FREECAD ASSEMBLY — COMPONENT RECIPES ("generated_example_K93-10436_all7_withDockLinkFrame")

This assembly document has 15 components, labeled P0..P14 below (a component is one placed body or linked part). 1 of them carries a construction recipe — the FreeCAD feature program that regenerates the part from scratch, quoted from this document or its linked companion documents; the rest are supplied as boundary geometry only. No exploded tour is included for this assembly.
COMPONENT P0 — geometry summary ("Body"; no construction recipe available for this part):
  bounding box: 104.0 x 36.0 x 1.5 mm
  tessellated surface: 8,624 triangles
  volume: 4912 mm^3 (87% of its bounding box)
  symmetry: mirror-symmetric across its y mid-plane
COMPONENT P1 — geometry summary ("Body001"; no construction recipe available for this part):
  bounding box: 36.0 x 20.0 x 8.6 mm
  tessellated surface: 3,058 triangles
  volume: 2231 mm^3 (36% of its bounding box)
COMPONENT P2 — geometry summary ("Body002"; no construction recipe available for this part):
  bounding box: 36.0 x 20.0 x 8.6 mm
  tessellated surface: 3,058 triangles
  volume: 2231 mm^3 (36% of its bounding box)
COMPONENT P3 — geometry summary ("Body003"; no construction recipe available for this part):
  bounding box: 36.0 x 20.0 x 8.6 mm
  tessellated surface: 3,058 triangles
  volume: 2231 mm^3 (36% of its bounding box)
COMPONENT P4 — geometry summary ("Body004"; no construction recipe available for this part):
  bounding box: 36.0 x 20.0 x 8.6 mm
  tessellated surface: 3,058 triangles
  volume: 2231 mm^3 (36% of its bounding box)
COMPONENT P5 — geometry summary ("Body005"; no construction recipe available for this part):
  bounding box: 121.4 x 53.2 x 25.0 mm
  tessellated surface: 7,988 triangles
  volume: 30997 mm^3 (19% of its bounding box)
COMPONENT P6 — recipe-attached ("Body (Mirror #1)", a linked part whose construction recipe lives in a companion FreeCAD document of the same project; that document's serialized recipe follows).
Construction recipe (the companion document, serialized — sketch geometry with constraints, then the solid features built on it; lengths are millimeters unless a unit is written):

FCSTD DOCUMENT  (FreeCAD 1.1R20251031 (Git shallow))
Label: K93-10436-H7-L120_DockLink_Frame_example_mirrored
License: All rights reserved
LicenseURL: https://en.wikipedia.org/wiki/All_rights_reserved
objects: App::Link×7, PartDesign::Chamfer×2, Assembly::JointGroup×1, Part::MultiFuse×1, App::Point×1, PartDesign::FeatureBase×1, PartDesign::Body×1, Part::Mirroring×1
note: 11 computed .brp shape members not serialized (recipe doc carries the construction recipe); baked Part::Feature solids carry a one-line shape summary decoded from their .brp
EXTERNAL_REF file=K93-10436-H7-L120_DockLink_Frame.FCStd obj=Body
EXTERNAL_REF file=../../FreeCAD_DElements/DockLink/DockLink_male.FCStd obj=Body
EXTERNAL_REF file=../../FreeCAD_DElements/DockLink/DockLink_female.FCStd obj=Body

FEATURE [Assembly::JointGroup] Joints
FEATURE [App::Link] K93_10436_H7_L120_DockLink_Frame  label="K93-10436-H7-L120_DockLink_Frame"
  LinkPlacement = pos=(0,-10.9,-10.9) rot=(1,0,0;1.5708rad)
  LinkedObject = -> <external K93-10436-H7-L120_DockLink_Frame.FCStd>#Body
  Placement = pos=(0,-10.9,-10.9) rot=(1,0,0;1.5708rad)
FEATURE [App::Link] Body_DockLink_male
  LinkPlacement = pos=(34.6042,3.94077e-06,-35) rot=(1,0,0;3.14159rad)
  LinkedObject = -> <external ../../FreeCAD_DElements/DockLink/DockLink_male.FCStd>#Body
  Placement = pos=(34.6042,3.94077e-06,-35) rot=(1,0,0;3.14159rad)
FEATURE [App::Link] Body_DockLink_male001
  LinkPlacement = pos=(-34.6042,3.94077e-06,-35) rot=(0,1,0;3.14159rad)
  LinkedObject = -> <external ../../FreeCAD_DElements/DockLink/DockLink_male.FCStd>#Body
  Placement = pos=(-34.6042,3.94077e-06,-35) rot=(0,1,0;3.14159rad)
FEATURE [App::Link] Body_DockLink_male002
  LinkPlacement = pos=(-58.2042,-1.22189e-07,-10.9) rot=(0,1,0;4.71239rad)
  LinkedObject = -> <external ../../FreeCAD_DElements/DockLink/DockLink_male.FCStd>#Body
  Placement = pos=(-58.2042,-1.22189e-07,-10.9) rot=(0,1,0;4.71239rad)
FEATURE [App::Link] Body_DockLink_female
  LinkPlacement = pos=(34.6042,-3.17362e-06,7.2) rot=(1,0,0;0rad)
  LinkedObject = -> <external ../../FreeCAD_DElements/DockLink/DockLink_female.FCStd>#Body
  Placement = pos=(34.6042,-3.17362e-06,7.2) rot=(1,0,0;0rad)
FEATURE [App::Link] Body_DockLink_female002
  LinkPlacement = pos=(-34.6042,-3.17362e-06,7.2) rot=(1,0,0;0rad)
  LinkedObject = -> <external ../../FreeCAD_DElements/DockLink/DockLink_female.FCStd>#Body
  Placement = pos=(-34.6042,-3.17362e-06,7.2) rot=(1,0,0;0rad)
FEATURE [App::Link] Body_DockLink_female003
  LinkPlacement = pos=(52.2042,-1.22189e-07,-10.9) rot=(0,1,0;1.5708rad)
  LinkedObject = -> <external ../../FreeCAD_DElements/DockLink/DockLink_female.FCStd>#Body
  Placement = pos=(52.2042,-1.22189e-07,-10.9) rot=(0,1,0;1.5708rad)
FEATURE [Part::MultiFuse] Fusion
  Refine = true
  Shapes = -> [K93_10436_H7_L120_DockLink_Frame,Body_DockLink_male,Body_DockLink_male001,Body_DockLink_male002,Body_DockLink_female,Body_DockLink_female002,Body_DockLink_female003]
FEATURE [App::Point] Origin005  label="Origin006"
  Role = Origin
FEATURE [PartDesign::FeatureBase] BaseFeature
  BaseFeature = -> Fusion
  Suppressed = false
FEATURE [PartDesign::Chamfer] Chamfer
  Angle = 45
  Base = -> BaseFeature [Edge186,Edge341,Edge191,Edge207,Edge211,Edge212,Edge219,Edge234,Edge349,Edge348,Edge347,Edge346,Edge345,Edge344,Edge343,Edge342,Edge236,Edge221,Edge214,Edge210,Edge206,Edge193,Edge184,Edge494,Edge376,Edge367,Edge356,Edge354,Edge350,Edge357,Edge365,Edge493,Edge49]
  BaseFeature = -> BaseFeature
  ChamferType = 0
  FlipDirection = false
  Refine = true
  Size = 1
  Size2 = 1
  SupportTransform = false
  Suppressed = false
  UseAllEdges = false
FEATURE [PartDesign::Chamfer] Chamfer001
  Angle = 45
  Base = -> Chamfer [Edge351,Edge341,Edge338,Edge312,Edge308,Edge299,Edge287,Edge285,Edge289,Edge321,Edge325,Edge337]
  BaseFeature = -> Chamfer
  ChamferType = 0
  FlipDirection = false
  Refine = true
  Size = 1
  Size2 = 1
  SupportTransform = false
  Suppressed = false
  UseAllEdges = false
FEATURE [PartDesign::Body] Body
  AllowCompound = true
  BaseFeature = -> Fusion
  Group = -> [BaseFeature,Chamfer,Chamfer001]
  Origin = -> Origin004
  Tip = -> Chamfer001
FEATURE [Part::Mirroring] Part__Mirroring  label="Body (Mirror #1)"
  Base = (0,0,0)
  Normal = (0,1,0)
  Source = -> Body
COMPONENT P7 — geometry summary ("K93-120"; no construction recipe available for this part):
  bounding box: 121.5 x 104.0 x 36.0 mm
  tessellated surface: 9,940 triangles
  volume: 84663 mm^3 (19% of its bounding box)
  symmetry: 2-fold rotationally symmetric about the y axis; mirror-symmetric across its x mid-plane, z mid-plane
COMPONENT P8 — geometry summary ("Reference_all7 1"; no construction recipe available for this part):
  bounding box: 140.0 x 99.6 x 22.5 mm
  tessellated surface: 168,602 triangles
  volume: 30738 mm^3 (10% of its bounding box)
COMPONENT P9 — geometry summary ("3M_SJ5382"; no construction recipe available for this part):
  bounding box: 6.3 x 6.3 x 1.9 mm
  tessellated surface: 1,400 triangles
  volume: 39 mm^3 (52% of its bounding box)
  symmetry: 6-fold rotationally symmetric about the z axis; mirror-symmetric across its y mid-plane
COMPONENT P10 — geometry summary ("3M_SJ5383"; no construction recipe available for this part):
  bounding box: 6.3 x 6.3 x 1.9 mm
  tessellated surface: 1,400 triangles
  volume: 39 mm^3 (52% of its bounding box)
  symmetry: 6-fold rotationally symmetric about the z axis; mirror-symmetric across its y mid-plane
COMPONENT P11 — geometry summary ("3M_SJ5384"; no construction recipe available for this part):
  bounding box: 6.3 x 6.3 x 1.9 mm
  tessellated surface: 1,400 triangles
  volume: 39 mm^3 (52% of its bounding box)
  symmetry: 6-fold rotationally symmetric about the z axis; mirror-symmetric across its y mid-plane
COMPONENT P12 — geometry summary ("3M_SJ5385"; no construction recipe available for this part):
  bounding box: 6.3 x 6.3 x 1.9 mm
  tessellated surface: 1,400 triangles
  volume: 39 mm^3 (52% of its bounding box)
  symmetry: 6-fold rotationally symmetric about the z axis; mirror-symmetric across its y mid-plane
COMPONENT P13 — geometry summary ("3M_SJ5386"; no construction recipe available for this part):
  bounding box: 6.3 x 6.3 x 1.9 mm
  tessellated surface: 1,400 triangles
  volume: 39 mm^3 (52% of its bounding box)
  symmetry: 6-fold rotationally symmetric about the z axis; mirror-symmetric across its y mid-plane
COMPONENT P14 — geometry summary ("3M_SJ5387"; no construction recipe available for this part):
  bounding box: 6.3 x 6.3 x 1.9 mm
  tessellated surface: 1,400 triangles
  volume: 39 mm^3 (52% of its bounding box)
  symmetry: 6-fold rotationally symmetric about the z axis; mirror-symmetric across its y mid-plane
PROVENANCE & LICENSES
A FreeCAD (.FCStd) document from a public repository crawl; recipes are the document's own serialized feature recipes (and, for linked parts, companion documents' recipes).
License: mit.
